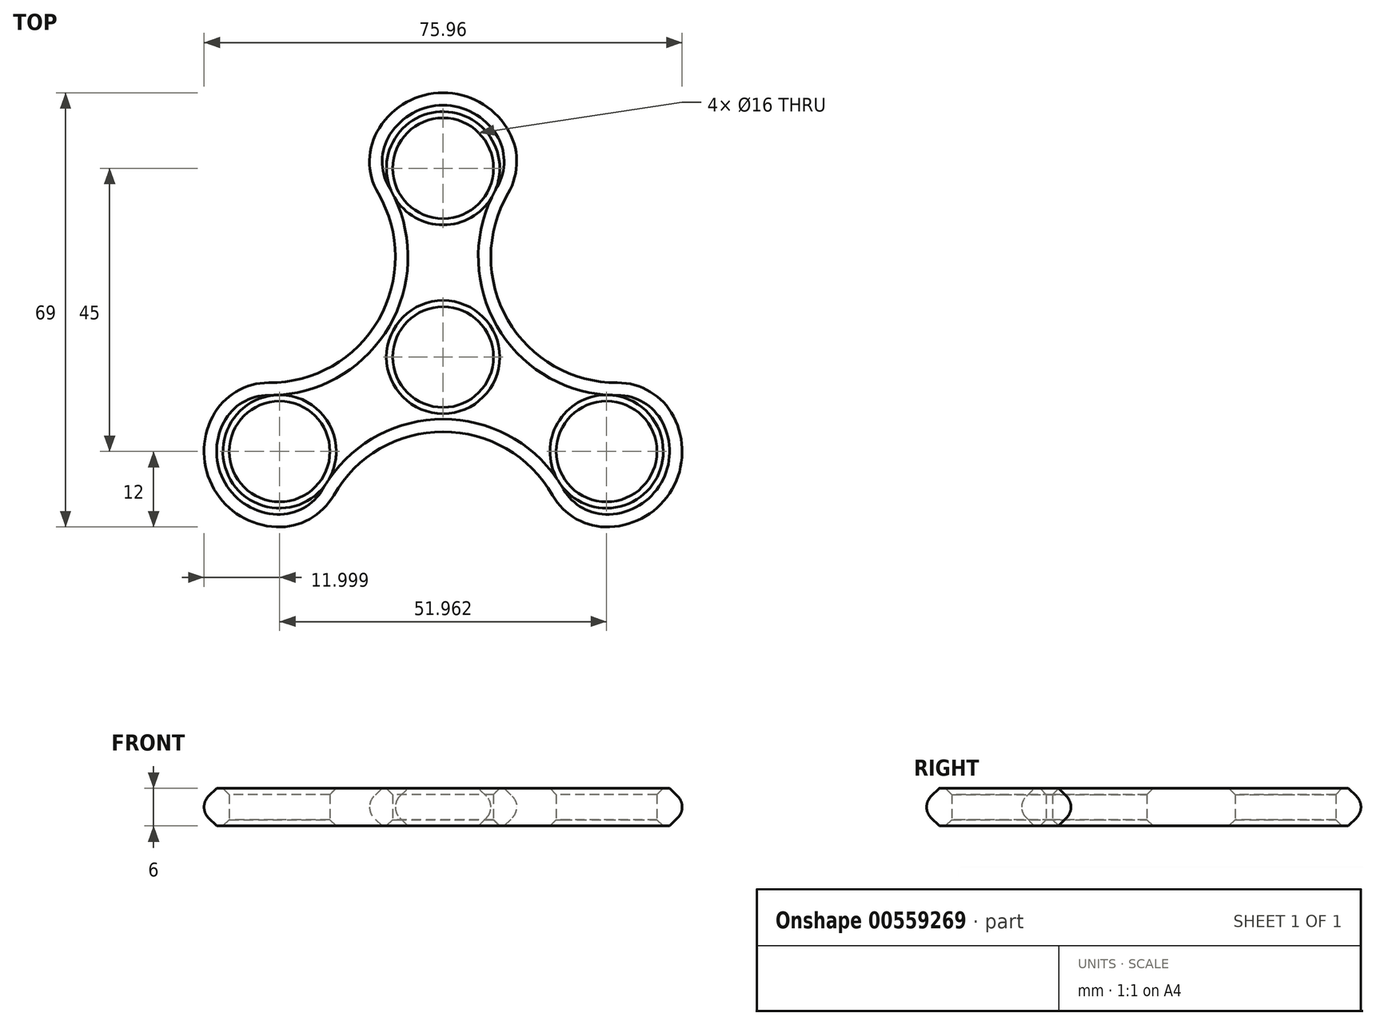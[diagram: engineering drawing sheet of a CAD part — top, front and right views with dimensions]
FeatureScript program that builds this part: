
annotation { "Feature Type Name" : "Feature", "Feature Type Description" : "" }
export const myFeature = defineFeature(function(context is Context, id is Id, definition is map)
    precondition{}
    {
        {
            var Q0;
            Q0=qCreatedBy(makeId("Top.planeOp"),FACE);
            var sketch = newSketch(context, id + "F0", { "sketchPlane" : qUnion([Q0])});
            skLineSegment(sketch, "E0", {"start": v(0, 0) * mm, "end": v(0, 42.37) * mm, "construction": true});
            skLineSegment(sketch, "E1.1.0", {"start": v(0, 0) * mm, "end": v(-36.7, -21.19) * mm, "construction": true});
            skLineSegment(sketch, "E1.2.0", {"start": v(0, 0) * mm, "end": v(36.7, -21.19) * mm, "construction": true});
            skPoint(sketch, "E1.center", {"position": v(0, 0) * mm});
            skCircle(sketch, "E2", {"center": v(0, 0) * mm, "radius": 8 * mm});
            skCircle(sketch, "E3", {"center": v(0, 30) * mm, "radius": 8 * mm});
            skLineSegment(sketch, "E4", {"start": v(-46.25, 0) * mm, "end": v(51.92, 0) * mm, "construction": true});
            skCircle(sketch, "E5.1.1", {"center": v(-25.98, -15) * mm, "radius": 8 * mm});
            skArc(sketch, "E5.2.0", {"start": v(26.47, -26.99) * mm, "mid": v(36.37, -21) * mm, "end": v(36.61, -9.43) * mm});
            skCircle(sketch, "E5.2.1", {"center": v(25.98, -15) * mm, "radius": 8 * mm});
            skPoint(sketch, "E6.orphan", {"position": v(-12, 0) * mm});
            skPoint(sketch, "E7.orphan", {"position": v(12, 0) * mm});
            skArc(sketch, "E8", {"start": v(-27.7, -4.07) * mm, "mid": v(-10.27, 5.93) * mm, "end": v(-10.32, 26.02) * mm});
            skArc(sketch, "E9.1.0", {"start": v(17.38, -21.95) * mm, "mid": v(0, -11.86) * mm, "end": v(-17.38, -21.95) * mm});
            skArc(sketch, "E9.2.0", {"start": v(10.32, 26.02) * mm, "mid": v(10.27, 5.93) * mm, "end": v(27.7, -4.07) * mm});
            skArc(sketch, "E10.trimOffspring", {"start": v(-36.61, -9.43) * mm, "mid": v(-36.37, -21) * mm, "end": v(-26.47, -26.99) * mm});
            skArc(sketch, "E11.trimOffspring", {"start": v(10.14, 36.42) * mm, "mid": v(0, 42) * mm, "end": v(-10.14, 36.42) * mm});
            skPoint(sketch, "E12.visualSharp", {"position": v(-11.88, 28.3) * mm});
            skArc(sketch, "E12.filletArc", {"start": v(-10.14, 36.42) * mm, "mid": v(-11.69, 31.25) * mm, "end": v(-10.32, 26.02) * mm});
            skPoint(sketch, "E13.visualSharp", {"position": v(11.88, 28.3) * mm});
            skArc(sketch, "E13.filletArc", {"start": v(10.32, 26.02) * mm, "mid": v(11.69, 31.25) * mm, "end": v(10.14, 36.42) * mm});
            skPoint(sketch, "E14.visualSharp", {"position": v(30.46, -3.87) * mm});
            skArc(sketch, "E14.filletArc", {"start": v(36.61, -9.43) * mm, "mid": v(32.9, -5.5) * mm, "end": v(27.7, -4.07) * mm});
            skPoint(sketch, "E15.visualSharp", {"position": v(18.58, -24.44) * mm});
            skArc(sketch, "E15.filletArc", {"start": v(17.38, -21.95) * mm, "mid": v(21.22, -25.75) * mm, "end": v(26.47, -26.99) * mm});
            skPoint(sketch, "E16.visualSharp", {"position": v(-18.58, -24.44) * mm});
            skArc(sketch, "E16.filletArc", {"start": v(-26.47, -26.99) * mm, "mid": v(-21.22, -25.75) * mm, "end": v(-17.38, -21.95) * mm});
            skPoint(sketch, "E17.visualSharp", {"position": v(-30.46, -3.87) * mm});
            skArc(sketch, "E17.filletArc", {"start": v(-27.7, -4.07) * mm, "mid": v(-32.9, -5.5) * mm, "end": v(-36.61, -9.43) * mm});
            skSolve(sketch);
        }
        {
            var Q0;
            Q0=makeQuery(id+"F0.imprint","IMPRINT",FACE,{"disambiguationData":[TD([[makeQuery(id+"F0.imprint","IMPRINT",EDGE,{"derivedFrom":sQuery(id+"F0.wireOp",EDGE,"E2")}),-1.0]])]});
            extrude(context, id + "F1", {"entities" : qUnion([Q0]), "depth" : 6 * mm, "offsetDistance" : 25 * mm});
        }
        {
            var Q0;
            Q0=makeQuery(id+"F1.opExtrude","CAP_EDGE",EDGE,{"disambiguationData":[OSD([sQuery(id+"F0.wireOp",EDGE,"E8")])],"isStart":false});
            var Q1;
            Q1=makeQuery(id+"F1.opExtrude","CAP_EDGE",EDGE,{"disambiguationData":[OSD([sQuery(id+"F0.wireOp",EDGE,"E12.filletArc")])],"isStart":false});
            var Q2;
            Q2=makeQuery(id+"F1.opExtrude","CAP_EDGE",EDGE,{"disambiguationData":[OSD([sQuery(id+"F0.wireOp",EDGE,"E11.trimOffspring")])],"isStart":false});
            var Q3;
            Q3=makeQuery(id+"F1.opExtrude","CAP_EDGE",EDGE,{"disambiguationData":[OSD([sQuery(id+"F0.wireOp",EDGE,"E13.filletArc")])],"isStart":false});
            var Q4;
            Q4=makeQuery(id+"F1.opExtrude","CAP_EDGE",EDGE,{"disambiguationData":[OSD([sQuery(id+"F0.wireOp",EDGE,"E9.2.0")])],"isStart":false});
            var Q5;
            Q5=makeQuery(id+"F1.opExtrude","CAP_EDGE",EDGE,{"disambiguationData":[OSD([sQuery(id+"F0.wireOp",EDGE,"E14.filletArc")])],"isStart":false});
            var Q6;
            Q6=makeQuery(id+"F1.opExtrude","CAP_EDGE",EDGE,{"disambiguationData":[OSD([sQuery(id+"F0.wireOp",EDGE,"E5.2.0")])],"isStart":false});
            var Q7;
            Q7=makeQuery(id+"F1.opExtrude","CAP_EDGE",EDGE,{"disambiguationData":[OSD([sQuery(id+"F0.wireOp",EDGE,"E15.filletArc")])],"isStart":false});
            var Q8;
            Q8=makeQuery(id+"F1.opExtrude","CAP_EDGE",EDGE,{"disambiguationData":[OSD([sQuery(id+"F0.wireOp",EDGE,"E9.1.0")])],"isStart":false});
            var Q9;
            Q9=makeQuery(id+"F1.opExtrude","CAP_EDGE",EDGE,{"disambiguationData":[OSD([sQuery(id+"F0.wireOp",EDGE,"E16.filletArc")])],"isStart":false});
            var Q10;
            Q10=makeQuery(id+"F1.opExtrude","CAP_EDGE",EDGE,{"disambiguationData":[OSD([sQuery(id+"F0.wireOp",EDGE,"E10.trimOffspring")])],"isStart":false});
            var Q11;
            Q11=makeQuery(id+"F1.opExtrude","CAP_EDGE",EDGE,{"disambiguationData":[OSD([sQuery(id+"F0.wireOp",EDGE,"E17.filletArc")])],"isStart":false});
            var Q12;
            Q12=makeQuery(id+"F1.opExtrude","CAP_EDGE",EDGE,{"disambiguationData":[OSD([sQuery(id+"F0.wireOp",EDGE,"E16.filletArc")])],"isStart":true});
            var Q13;
            Q13=makeQuery(id+"F1.opExtrude","CAP_EDGE",EDGE,{"disambiguationData":[OSD([sQuery(id+"F0.wireOp",EDGE,"E10.trimOffspring")])],"isStart":true});
            var Q14;
            Q14=makeQuery(id+"F1.opExtrude","CAP_EDGE",EDGE,{"disambiguationData":[OSD([sQuery(id+"F0.wireOp",EDGE,"E17.filletArc")])],"isStart":true});
            var Q15;
            Q15=makeQuery(id+"F1.opExtrude","CAP_EDGE",EDGE,{"disambiguationData":[OSD([sQuery(id+"F0.wireOp",EDGE,"E8")])],"isStart":true});
            var Q16;
            Q16=makeQuery(id+"F1.opExtrude","CAP_EDGE",EDGE,{"disambiguationData":[OSD([sQuery(id+"F0.wireOp",EDGE,"E12.filletArc")])],"isStart":true});
            var Q17;
            Q17=makeQuery(id+"F1.opExtrude","CAP_EDGE",EDGE,{"disambiguationData":[OSD([sQuery(id+"F0.wireOp",EDGE,"E9.1.0")])],"isStart":true});
            var Q18;
            Q18=makeQuery(id+"F1.opExtrude","CAP_EDGE",EDGE,{"disambiguationData":[OSD([sQuery(id+"F0.wireOp",EDGE,"E15.filletArc")])],"isStart":true});
            var Q19;
            Q19=makeQuery(id+"F1.opExtrude","CAP_EDGE",EDGE,{"disambiguationData":[OSD([sQuery(id+"F0.wireOp",EDGE,"E5.2.0")])],"isStart":true});
            var Q20;
            Q20=makeQuery(id+"F1.opExtrude","CAP_EDGE",EDGE,{"disambiguationData":[OSD([sQuery(id+"F0.wireOp",EDGE,"E14.filletArc")])],"isStart":true});
            var Q21;
            Q21=makeQuery(id+"F1.opExtrude","CAP_EDGE",EDGE,{"disambiguationData":[OSD([sQuery(id+"F0.wireOp",EDGE,"E9.2.0")])],"isStart":true});
            var Q22;
            Q22=makeQuery(id+"F1.opExtrude","CAP_EDGE",EDGE,{"disambiguationData":[OSD([sQuery(id+"F0.wireOp",EDGE,"E13.filletArc")])],"isStart":true});
            var Q23;
            Q23=makeQuery(id+"F1.opExtrude","CAP_EDGE",EDGE,{"disambiguationData":[OSD([sQuery(id+"F0.wireOp",EDGE,"E11.trimOffspring")])],"isStart":true});
            var Q24;
            Q24=makeQuery(id+"F1.opExtrude","SWEPT_FACE",FACE,{"disambiguationData":[OSD([sQuery(id+"F0.wireOp",EDGE,"E9.2.0")])]});
            chamfer(context, id + "F2", {"entities" : qUnion([Q0, Q1, Q2, Q3, Q4, Q5, Q6, Q7, Q8, Q9, Q10, Q11, Q12, Q13, Q14, Q15, Q16, Q17, Q18, Q19, Q20, Q21, Q22, Q23, Q24]), "width" : 2 * mm, "tangentPropagation" : true});
        }
        {
            var Q0;
            Q0=makeQuery(id+"F1.opExtrude","SWEPT_FACE",FACE,{"disambiguationData":[OSD([sQuery(id+"F0.wireOp",EDGE,"E9.2.0")])]});
            var Q1;
            Q1=makeQuery(id+"F1.opExtrude","SWEPT_FACE",FACE,{"disambiguationData":[OSD([sQuery(id+"F0.wireOp",EDGE,"E14.filletArc")])]});
            var Q2;
            Q2=makeQuery(id+"F1.opExtrude","SWEPT_FACE",FACE,{"disambiguationData":[OSD([sQuery(id+"F0.wireOp",EDGE,"E5.2.0")])]});
            var Q3;
            Q3=makeQuery(id+"F1.opExtrude","SWEPT_FACE",FACE,{"disambiguationData":[OSD([sQuery(id+"F0.wireOp",EDGE,"E15.filletArc")])]});
            var Q4;
            Q4=makeQuery(id+"F1.opExtrude","SWEPT_FACE",FACE,{"disambiguationData":[OSD([sQuery(id+"F0.wireOp",EDGE,"E9.1.0")])]});
            var Q5;
            Q5=makeQuery(id+"F1.opExtrude","SWEPT_FACE",FACE,{"disambiguationData":[OSD([sQuery(id+"F0.wireOp",EDGE,"E16.filletArc")])]});
            var Q6;
            Q6=makeQuery(id+"F1.opExtrude","SWEPT_FACE",FACE,{"disambiguationData":[OSD([sQuery(id+"F0.wireOp",EDGE,"E10.trimOffspring")])]});
            var Q7;
            Q7=makeQuery(id+"F1.opExtrude","SWEPT_FACE",FACE,{"disambiguationData":[OSD([sQuery(id+"F0.wireOp",EDGE,"E17.filletArc")])]});
            var Q8;
            Q8=makeQuery(id+"F1.opExtrude","SWEPT_FACE",FACE,{"disambiguationData":[OSD([sQuery(id+"F0.wireOp",EDGE,"E8")])]});
            var Q9;
            Q9=makeQuery(id+"F1.opExtrude","SWEPT_FACE",FACE,{"disambiguationData":[OSD([sQuery(id+"F0.wireOp",EDGE,"E12.filletArc")])]});
            var Q10;
            Q10=makeQuery(id+"F1.opExtrude","SWEPT_FACE",FACE,{"disambiguationData":[OSD([sQuery(id+"F0.wireOp",EDGE,"E11.trimOffspring")])]});
            var Q11;
            Q11=makeQuery(id+"F1.opExtrude","SWEPT_FACE",FACE,{"disambiguationData":[OSD([sQuery(id+"F0.wireOp",EDGE,"E13.filletArc")])]});
            fillet(context, id + "F3", {"entities" : qUnion([Q0, Q1, Q2, Q3, Q4, Q5, Q6, Q7, Q8, Q9, Q10, Q11]), "radius" : 2.4 * mm, "allowEdgeOverflow" : false});
        }
        {
            var Q0;
            Q0=makeQuery(id+"F1.opExtrude","SWEPT_FACE",FACE,{"disambiguationData":[OSD([sQuery(id+"F0.wireOp",EDGE,"E3")])]});
            var Q1;
            Q1=makeQuery(id+"F1.opExtrude","SWEPT_FACE",FACE,{"disambiguationData":[OSD([sQuery(id+"F0.wireOp",EDGE,"E5.2.1")])]});
            var Q2;
            Q2=makeQuery(id+"F1.opExtrude","SWEPT_FACE",FACE,{"disambiguationData":[OSD([sQuery(id+"F0.wireOp",EDGE,"E2")])]});
            var Q3;
            Q3=makeQuery(id+"F1.opExtrude","SWEPT_FACE",FACE,{"disambiguationData":[OSD([sQuery(id+"F0.wireOp",EDGE,"E5.1.1")])]});
            chamfer(context, id + "F4", {"entities" : qUnion([Q0, Q1, Q2, Q3]), "width" : 1 * mm, "tangentPropagation" : true});
        }
    });
